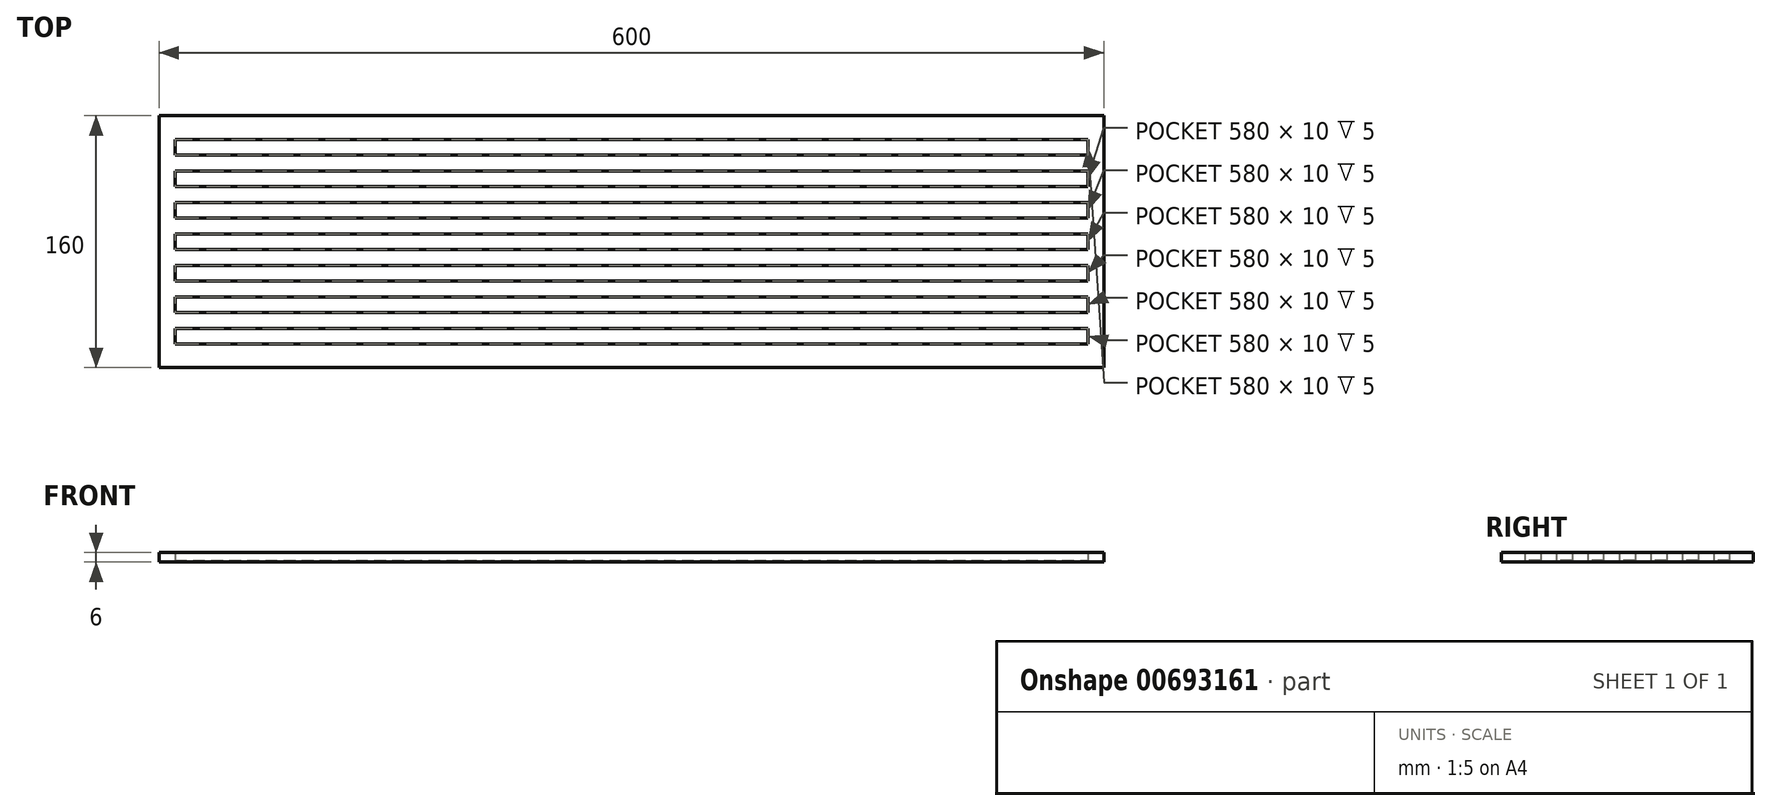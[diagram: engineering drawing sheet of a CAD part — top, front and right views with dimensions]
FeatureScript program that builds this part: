
annotation { "Feature Type Name" : "Feature", "Feature Type Description" : "" }
export const myFeature = defineFeature(function(context is Context, id is Id, definition is map)
    precondition{}
    {
        {
            var Q0;
            Q0=qCreatedBy(makeId("Top.planeOp"),FACE);
            var sketch = newSketch(context, id + "F0", { "sketchPlane" : qUnion([Q0])});
            skLineSegment(sketch, "E0.bottom", {"start": v(-289.97, 36.74) * mm, "end": v(310.03, 36.74) * mm});
            skLineSegment(sketch, "E0.top", {"start": v(-289.97, -123.26) * mm, "end": v(310.03, -123.26) * mm});
            skLineSegment(sketch, "E0.left", {"start": v(-289.97, 36.74) * mm, "end": v(-289.97, -123.26) * mm});
            skLineSegment(sketch, "E0.right", {"start": v(310.03, 36.74) * mm, "end": v(310.03, -123.26) * mm});
            skLineSegment(sketch, "E1.bottom", {"start": v(-279.97, 21.74) * mm, "end": v(300.03, 21.74) * mm});
            skLineSegment(sketch, "E1.top", {"start": v(-279.97, 11.74) * mm, "end": v(300.03, 11.74) * mm});
            skLineSegment(sketch, "E1.left", {"start": v(-279.97, 21.74) * mm, "end": v(-279.97, 11.74) * mm});
            skLineSegment(sketch, "E1.right", {"start": v(300.03, 21.74) * mm, "end": v(300.03, 11.74) * mm});
            skLineSegment(sketch, "E2.0.1.0", {"start": v(300.03, 1.74) * mm, "end": v(300.03, -8.26) * mm});
            skLineSegment(sketch, "E2.0.1.1", {"start": v(-279.97, 1.74) * mm, "end": v(300.03, 1.74) * mm});
            skLineSegment(sketch, "E2.0.1.2", {"start": v(-279.97, -8.26) * mm, "end": v(300.03, -8.26) * mm});
            skLineSegment(sketch, "E2.0.1.3", {"start": v(-279.97, 1.74) * mm, "end": v(-279.97, -8.26) * mm});
            skLineSegment(sketch, "E2.0.2.0", {"start": v(300.03, -18.26) * mm, "end": v(300.03, -28.26) * mm});
            skLineSegment(sketch, "E2.0.2.1", {"start": v(-279.97, -18.26) * mm, "end": v(300.03, -18.26) * mm});
            skLineSegment(sketch, "E2.0.2.2", {"start": v(-279.97, -28.26) * mm, "end": v(300.03, -28.26) * mm});
            skLineSegment(sketch, "E2.0.2.3", {"start": v(-279.97, -18.26) * mm, "end": v(-279.97, -28.26) * mm});
            skLineSegment(sketch, "E2.0.3.0", {"start": v(300.03, -38.26) * mm, "end": v(300.03, -48.26) * mm});
            skLineSegment(sketch, "E2.0.3.1", {"start": v(-279.97, -38.26) * mm, "end": v(300.03, -38.26) * mm});
            skLineSegment(sketch, "E2.0.3.2", {"start": v(-279.97, -48.26) * mm, "end": v(300.03, -48.26) * mm});
            skLineSegment(sketch, "E2.0.3.3", {"start": v(-279.97, -38.26) * mm, "end": v(-279.97, -48.26) * mm});
            skLineSegment(sketch, "E2.0.4.0", {"start": v(300.03, -58.26) * mm, "end": v(300.03, -68.26) * mm});
            skLineSegment(sketch, "E2.0.4.1", {"start": v(-279.97, -58.26) * mm, "end": v(300.03, -58.26) * mm});
            skLineSegment(sketch, "E2.0.4.2", {"start": v(-279.97, -68.26) * mm, "end": v(300.03, -68.26) * mm});
            skLineSegment(sketch, "E2.0.4.3", {"start": v(-279.97, -58.26) * mm, "end": v(-279.97, -68.26) * mm});
            skLineSegment(sketch, "E2.0.5.0", {"start": v(300.03, -78.26) * mm, "end": v(300.03, -88.26) * mm});
            skLineSegment(sketch, "E2.0.5.1", {"start": v(-279.97, -78.26) * mm, "end": v(300.03, -78.26) * mm});
            skLineSegment(sketch, "E2.0.5.2", {"start": v(-279.97, -88.26) * mm, "end": v(300.03, -88.26) * mm});
            skLineSegment(sketch, "E2.0.5.3", {"start": v(-279.97, -78.26) * mm, "end": v(-279.97, -88.26) * mm});
            skLineSegment(sketch, "E2.0.6.0", {"start": v(300.03, -98.26) * mm, "end": v(300.03, -108.26) * mm});
            skLineSegment(sketch, "E2.0.6.1", {"start": v(-279.97, -98.26) * mm, "end": v(300.03, -98.26) * mm});
            skLineSegment(sketch, "E2.0.6.2", {"start": v(-279.97, -108.26) * mm, "end": v(300.03, -108.26) * mm});
            skLineSegment(sketch, "E2.0.6.3", {"start": v(-279.97, -98.26) * mm, "end": v(-279.97, -108.26) * mm});
            skLineSegment(sketch, "E2.direction1", {"start": v(300.03, 11.74) * mm, "end": v(325.03, 11.74) * mm, "construction": true});
            skLineSegment(sketch, "E2.direction2", {"start": v(300.03, 11.74) * mm, "end": v(300.03, -8.26) * mm, "construction": true});
            skSolve(sketch);
        }
        {
            var Q0;
            Q0 = qSketchRegion(id + "F0", true);
            extrude(context, id + "F1", {"entities" : qUnion([Q0]), "depth" : 5 * mm, "offsetDistance" : 25 * mm});
        }
        {
            var Q0;
            Q0=makeQuery(id+"F1.opExtrude","CAP_FACE",FACE,{"disambiguationData":[OSD([sQuery(id+"F0.wireOp",EDGE,"E0.bottom"),sQuery(id+"F0.wireOp",EDGE,"E0.top"),sQuery(id+"F0.wireOp",EDGE,"E0.left"),sQuery(id+"F0.wireOp",EDGE,"E0.right"),sQuery(id+"F0.wireOp",EDGE,"E1.bottom"),sQuery(id+"F0.wireOp",EDGE,"E1.top"),sQuery(id+"F0.wireOp",EDGE,"E1.left"),sQuery(id+"F0.wireOp",EDGE,"E1.right"),sQuery(id+"F0.wireOp",EDGE,"E2.0.1.0"),sQuery(id+"F0.wireOp",EDGE,"E2.0.1.1"),sQuery(id+"F0.wireOp",EDGE,"E2.0.1.2"),sQuery(id+"F0.wireOp",EDGE,"E2.0.1.3"),sQuery(id+"F0.wireOp",EDGE,"E2.0.2.0"),sQuery(id+"F0.wireOp",EDGE,"E2.0.2.1"),sQuery(id+"F0.wireOp",EDGE,"E2.0.2.2"),sQuery(id+"F0.wireOp",EDGE,"E2.0.2.3"),sQuery(id+"F0.wireOp",EDGE,"E2.0.3.0"),sQuery(id+"F0.wireOp",EDGE,"E2.0.3.1"),sQuery(id+"F0.wireOp",EDGE,"E2.0.3.2"),sQuery(id+"F0.wireOp",EDGE,"E2.0.3.3"),sQuery(id+"F0.wireOp",EDGE,"E2.0.4.0"),sQuery(id+"F0.wireOp",EDGE,"E2.0.4.1"),sQuery(id+"F0.wireOp",EDGE,"E2.0.4.2"),sQuery(id+"F0.wireOp",EDGE,"E2.0.4.3"),sQuery(id+"F0.wireOp",EDGE,"E2.0.5.0"),sQuery(id+"F0.wireOp",EDGE,"E2.0.5.1"),sQuery(id+"F0.wireOp",EDGE,"E2.0.5.2"),sQuery(id+"F0.wireOp",EDGE,"E2.0.5.3"),sQuery(id+"F0.wireOp",EDGE,"E2.0.6.0"),sQuery(id+"F0.wireOp",EDGE,"E2.0.6.1"),sQuery(id+"F0.wireOp",EDGE,"E2.0.6.2"),sQuery(id+"F0.wireOp",EDGE,"E2.0.6.3")])],"isStart":true});
            var sketch = newSketch(context, id + "F2", { "sketchPlane" : qUnion([Q0])});
            skLineSegment(sketch, "E3.bottom", {"start": v(-289.97, -36.74) * mm, "end": v(310.03, -36.74) * mm});
            skLineSegment(sketch, "E3.top", {"start": v(-289.97, 123.26) * mm, "end": v(310.03, 123.26) * mm});
            skLineSegment(sketch, "E3.left", {"start": v(-289.97, -36.74) * mm, "end": v(-289.97, 123.26) * mm});
            skLineSegment(sketch, "E3.right", {"start": v(310.03, -36.74) * mm, "end": v(310.03, 123.26) * mm});
            skSolve(sketch);
        }
        {
            var Q0;
            Q0 = qSketchRegion(id + "F2", true);
            extrude(context, id + "F3", {"entities" : qUnion([Q0]), "operationType" : NewBodyOperationType.ADD, "depth" : 1 * mm, "offsetDistance" : 25 * mm});
        }
    });
